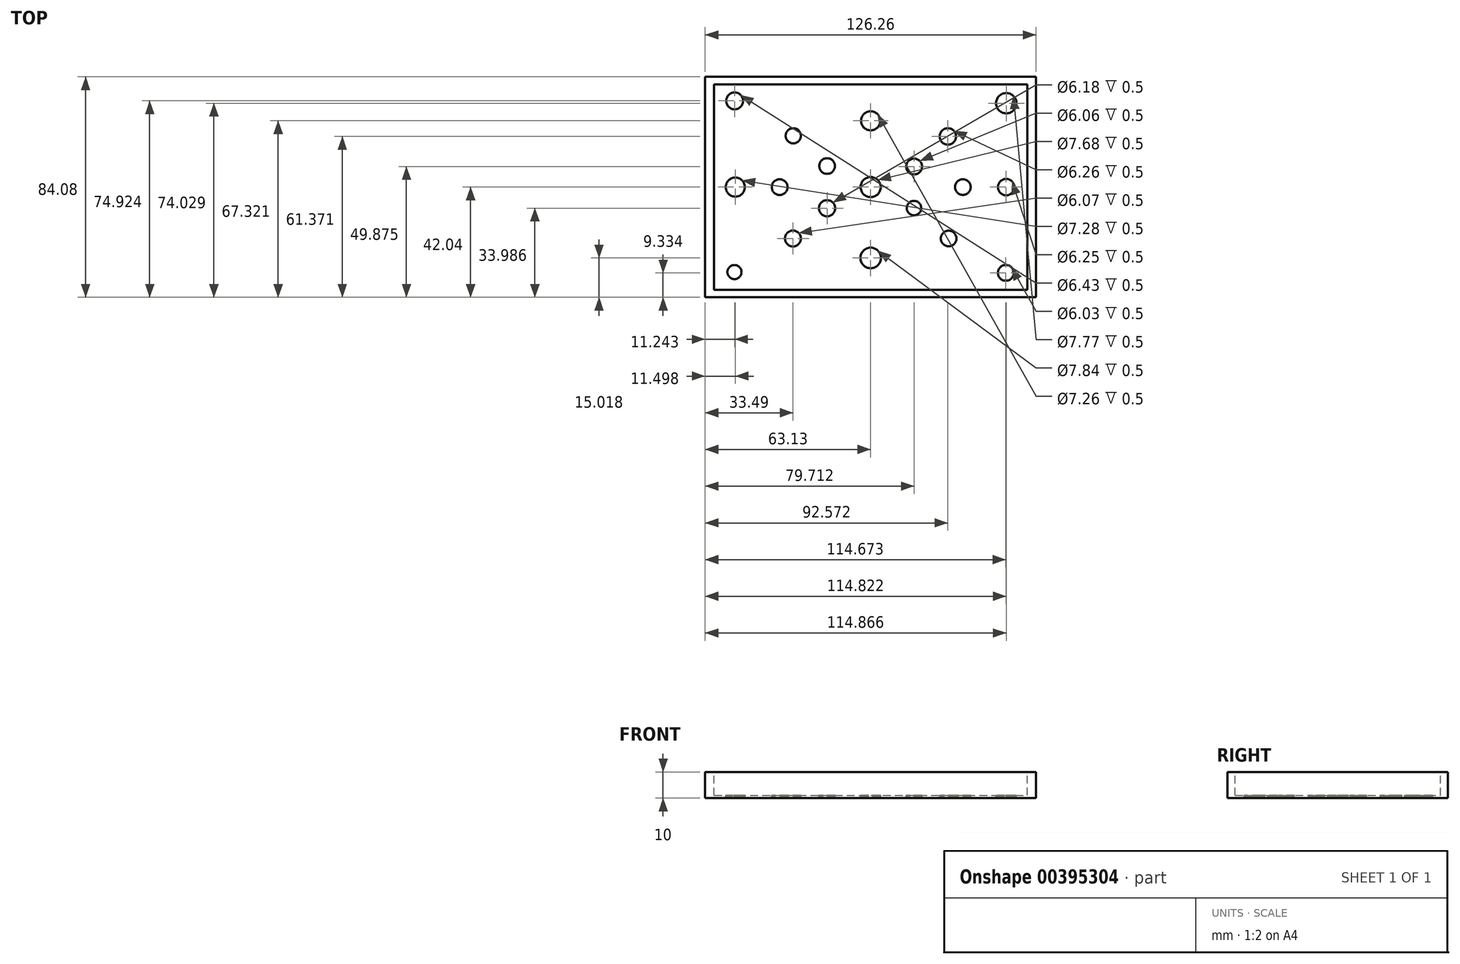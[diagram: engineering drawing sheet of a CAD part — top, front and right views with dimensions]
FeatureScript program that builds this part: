
annotation { "Feature Type Name" : "Feature", "Feature Type Description" : "" }
export const myFeature = defineFeature(function(context is Context, id is Id, definition is map)
    precondition{}
    {
        {
            var Q0;
            Q0=qCreatedBy(makeId("Top.planeOp"),FACE);
            var sketch = newSketch(context, id + "F0", { "sketchPlane" : qUnion([Q0])});
            skLineSegment(sketch, "E0.bottom", {"start": v(63.13, 42.04) * mm, "end": v(-63.13, 42.04) * mm});
            skLineSegment(sketch, "E0.top", {"start": v(63.13, -42.04) * mm, "end": v(-63.13, -42.04) * mm});
            skLineSegment(sketch, "E0.left", {"start": v(63.13, 42.04) * mm, "end": v(63.13, -42.04) * mm});
            skLineSegment(sketch, "E0.right", {"start": v(-63.13, 42.04) * mm, "end": v(-63.13, -42.04) * mm});
            skPoint(sketch, "E0.middle", {"position": v(0, 0) * mm});
            skSolve(sketch);
        }
        {
            var Q0;
            Q0 = qSketchRegion(id + "F0", true);
            extrude(context, id + "F1", {"entities" : qUnion([Q0]), "oppositeDirection" : true, "depth" : 10 * mm});
        }
        {
            var Q0;
            Q0=qCreatedBy(makeId("Top.planeOp"),FACE);
            var sketch = newSketch(context, id + "F2", { "sketchPlane" : qUnion([Q0])});
            skLineSegment(sketch, "E1.bottom", {"start": v(-59.73, -39.22) * mm, "end": v(59.73, -39.22) * mm});
            skLineSegment(sketch, "E1.top", {"start": v(-59.73, 39.22) * mm, "end": v(59.73, 39.22) * mm});
            skLineSegment(sketch, "E1.left", {"start": v(-59.73, -39.22) * mm, "end": v(-59.73, 39.22) * mm});
            skLineSegment(sketch, "E1.right", {"start": v(59.73, -39.22) * mm, "end": v(59.73, 39.22) * mm});
            skPoint(sketch, "E1.middle", {"position": v(0, 0) * mm});
            skSolve(sketch);
        }
        {
            var Q0;
            Q0 = qSketchRegion(id + "F2", true);
            extrude(context, id + "F3", {"entities" : qUnion([Q0]), "operationType" : NewBodyOperationType.REMOVE, "oppositeDirection" : true, "depth" : 9 * mm});
        }
        {
            var Q0;
            Q0=qCreatedBy(makeId("Top.planeOp"),FACE);
            var sketch = newSketch(context, id + "F4", { "sketchPlane" : qUnion([Q0])});
            skCircle(sketch, "E2", {"center": v(0, 0) * mm, "radius": 3.84 * mm});
            skSolve(sketch);
        }
        {
            var Q0;
            Q0=qCreatedBy(makeId("Top.planeOp"),FACE);
            var sketch = newSketch(context, id + "F5", { "sketchPlane" : qUnion([Q0])});
            skCircle(sketch, "E3", {"center": v(16.58, 7.83) * mm, "radius": 3.03 * mm});
            skSolve(sketch);
        }
        {
            var Q0;
            Q0=qCreatedBy(makeId("Top.planeOp"),FACE);
            var sketch = newSketch(context, id + "F6", { "sketchPlane" : qUnion([Q0])});
            skCircle(sketch, "E4", {"center": v(16.52, -8.01) * mm, "radius": 2.76 * mm});
            skCircle(sketch, "E5", {"center": v(-16.62, -8.05) * mm, "radius": 3.09 * mm});
            skCircle(sketch, "E6", {"center": v(-16.62, 8.04) * mm, "radius": 2.99 * mm});
            skSolve(sketch);
        }
        {
            var Q0;
            Q0 = qSketchRegion(id + "F6", true);
            extrude(context, id + "F7", {"entities" : qUnion([Q0]), "operationType" : NewBodyOperationType.REMOVE, "oppositeDirection" : true, "depth" : 9.5 * mm});
        }
        {
            var Q0;
            Q0 = qSketchRegion(id + "Fs7AzN1cLB0RIoi_1", true);
            var Q1;
            Q1 = qSketchRegion(id + "F5", true);
            extrude(context, id + "F8", {"entities" : qUnion([Q0, Q1]), "operationType" : NewBodyOperationType.REMOVE, "oppositeDirection" : true, "depth" : 9.5 * mm});
        }
        {
            var Q0;
            Q0 = qSketchRegion(id + "F4", true);
            var Q1;
            Q1=sQuery(id+"F4.wireOp",EDGE,"E2");
            extrude(context, id + "F9", {"entities" : qUnion([Q0]), "operationType" : NewBodyOperationType.REMOVE, "surfaceEntities" : qUnion([Q1]), "oppositeDirection" : true, "depth" : 9.5 * mm});
        }
        {
            var Q0;
            Q0=makeQuery(id+"F2.imprint","IMPRINT",FACE,{"disambiguationData":[TD([[makeQuery(id+"F2.imprint","IMPRINT",EDGE,{"derivedFrom":sQuery(id+"F2.wireOp",EDGE,"E1.bottom")}),1.0]])]});
            var sketch = newSketch(context, id + "F10", { "sketchPlane" : qUnion([Q0])});
            skCircle(sketch, "E7", {"center": v(29.44, 19.33) * mm, "radius": 3.13 * mm});
            skCircle(sketch, "E8", {"center": v(29.75, -19.61) * mm, "radius": 3 * mm});
            skCircle(sketch, "E9", {"center": v(-29.64, -19.61) * mm, "radius": 3.04 * mm});
            skCircle(sketch, "E10", {"center": v(-29.52, 19.57) * mm, "radius": 2.9 * mm});
            skSolve(sketch);
        }
        {
            var Q0;
            Q0 = qSketchRegion(id + "F10", true);
            extrude(context, id + "F11", {"entities" : qUnion([Q0]), "operationType" : NewBodyOperationType.REMOVE, "oppositeDirection" : true, "depth" : 9.5 * mm});
        }
        {
            var Q0;
            Q0=qCreatedBy(makeId("Top.planeOp"),FACE);
            var sketch = newSketch(context, id + "F12", { "sketchPlane" : qUnion([Q0])});
            skCircle(sketch, "E11", {"center": v(-51.89, 32.88) * mm, "radius": 3.22 * mm});
            skCircle(sketch, "E12", {"center": v(-51.94, -32.4) * mm, "radius": 2.68 * mm});
            skCircle(sketch, "E13", {"center": v(51.54, -32.7) * mm, "radius": 3.01 * mm});
            skCircle(sketch, "E14", {"center": v(51.74, 31.99) * mm, "radius": 3.89 * mm});
            skSolve(sketch);
        }
        {
            var Q0;
            Q0=qCreatedBy(makeId("Top.planeOp"),FACE);
            var sketch = newSketch(context, id + "F13", { "sketchPlane" : qUnion([Q0])});
            skCircle(sketch, "E15", {"center": v(-34.71, 0) * mm, "radius": 3 * mm});
            skCircle(sketch, "E16", {"center": v(35.18, 0) * mm, "radius": 2.98 * mm});
            skCircle(sketch, "E17", {"center": v(-51.63, 0) * mm, "radius": 3.64 * mm});
            skCircle(sketch, "E18", {"center": v(51.7, 0) * mm, "radius": 3.13 * mm});
            skSolve(sketch);
        }
        {
            var Q0;
            Q0 = qSketchRegion(id + "F13", true);
            extrude(context, id + "F14", {"entities" : qUnion([Q0]), "operationType" : NewBodyOperationType.REMOVE, "oppositeDirection" : true, "depth" : 9.5 * mm});
        }
        {
            var Q0;
            Q0 = qSketchRegion(id + "F12", true);
            extrude(context, id + "F15", {"entities" : qUnion([Q0]), "operationType" : NewBodyOperationType.REMOVE, "oppositeDirection" : true, "depth" : 9.5 * mm});
        }
        {
            var Q0;
            Q0=qCreatedBy(makeId("Top.planeOp"),FACE);
            var sketch = newSketch(context, id + "F16", { "sketchPlane" : qUnion([Q0])});
            skCircle(sketch, "E19", {"center": v(0, 25.28) * mm, "radius": 3.63 * mm});
            skCircle(sketch, "E20", {"center": v(0, -27.02) * mm, "radius": 3.92 * mm});
            skSolve(sketch);
        }
        {
            var Q0;
            Q0 = qSketchRegion(id + "F16", true);
            extrude(context, id + "F17", {"entities" : qUnion([Q0]), "operationType" : NewBodyOperationType.REMOVE, "oppositeDirection" : true, "depth" : 9.5 * mm});
        }
    });
